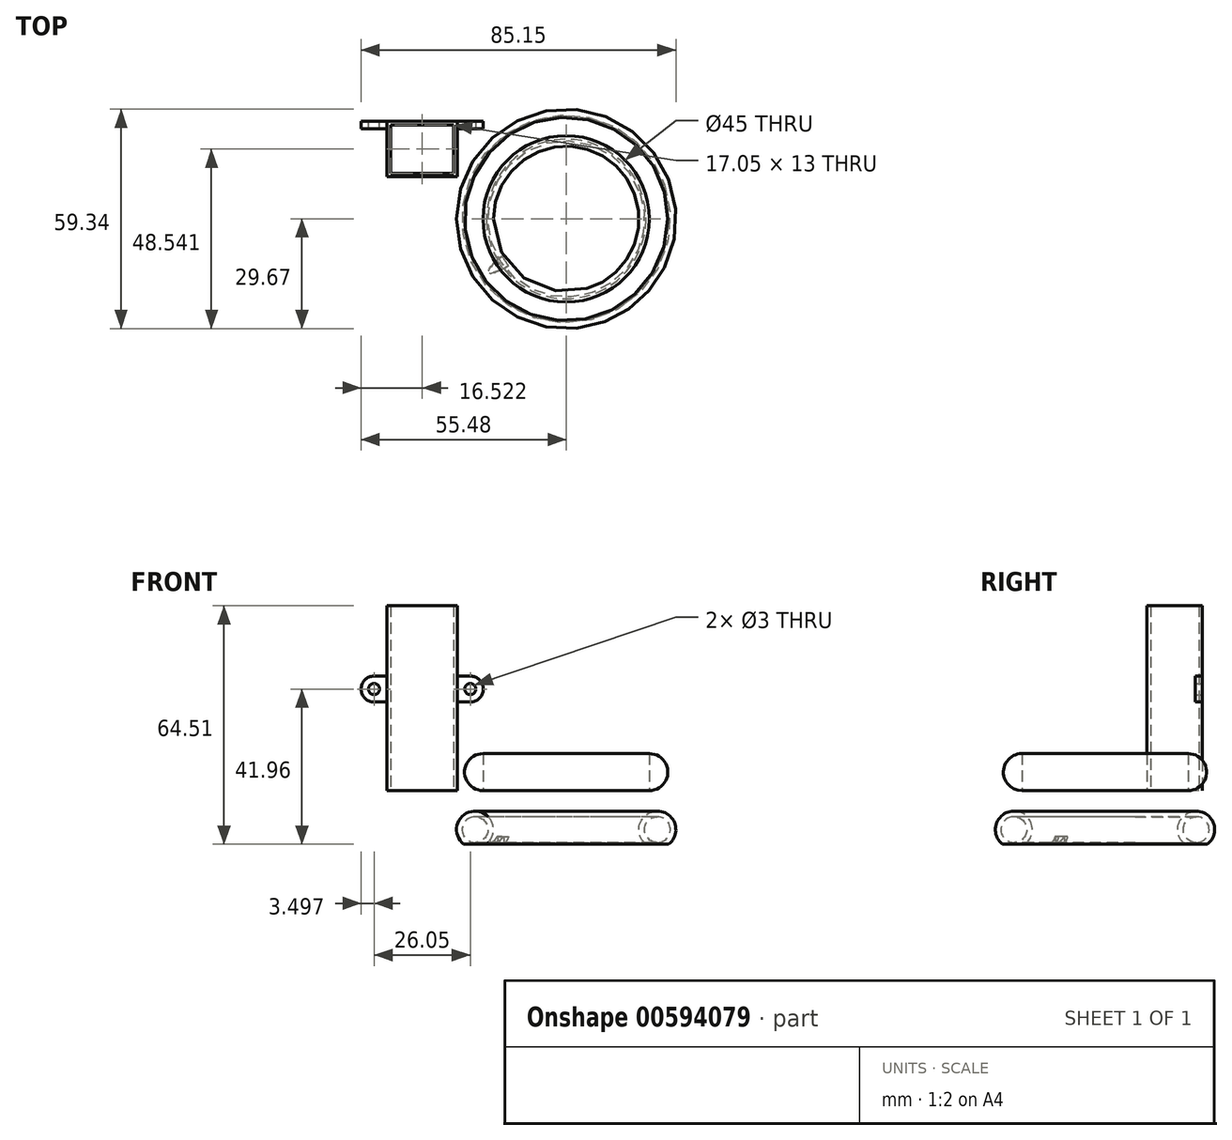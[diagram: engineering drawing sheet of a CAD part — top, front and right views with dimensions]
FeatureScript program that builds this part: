
annotation { "Feature Type Name" : "Feature", "Feature Type Description" : "" }
export const myFeature = defineFeature(function(context is Context, id is Id, definition is map)
    precondition{}
    {
        {
            var Q0;
            Q0=qCreatedBy(makeId("Top.planeOp"),FACE);
            var sketch = newSketch(context, id + "F0", { "sketchPlane" : qUnion([Q0])});
            skLineSegment(sketch, "E0.bottom", {"start": v(-48.48, 26.37) * mm, "end": v(-29.43, 26.37) * mm});
            skLineSegment(sketch, "E0.top", {"start": v(-48.48, 11.37) * mm, "end": v(-29.43, 11.37) * mm});
            skLineSegment(sketch, "E0.left", {"start": v(-48.48, 26.37) * mm, "end": v(-48.48, 11.37) * mm});
            skLineSegment(sketch, "E0.right", {"start": v(-29.43, 26.37) * mm, "end": v(-29.43, 11.37) * mm});
            skSolve(sketch);
        }
        {
            var Q0;
            Q0=makeQuery(id+"F0.imprint","IMPRINT",FACE,{"disambiguationData":[TD([[makeQuery(id+"F0.imprint","IMPRINT",EDGE,{"derivedFrom":sQuery(id+"F0.wireOp",EDGE,"E0.bottom")}),-1.0]])]});
            extrude(context, id + "F1", {"entities" : qUnion([Q0]), "depth" : 50 * mm, "offsetDistance" : 25 * mm});
        }
        {
            var Q0;
            Q0=makeQuery(id+"F1.opExtrude","CAP_FACE",FACE,{"disambiguationData":[OSD([sQuery(id+"F0.wireOp",EDGE,"E0.bottom"),sQuery(id+"F0.wireOp",EDGE,"E0.top"),sQuery(id+"F0.wireOp",EDGE,"E0.left"),sQuery(id+"F0.wireOp",EDGE,"E0.right")])],"isStart":false});
            var Q1;
            Q1=makeQuery(id+"F1.opExtrude","CAP_FACE",FACE,{"disambiguationData":[OSD([sQuery(id+"F0.wireOp",EDGE,"E0.bottom"),sQuery(id+"F0.wireOp",EDGE,"E0.top"),sQuery(id+"F0.wireOp",EDGE,"E0.left"),sQuery(id+"F0.wireOp",EDGE,"E0.right")])],"isStart":true});
            shell(context, id + "F2", {"entities" : qUnion([Q0, Q1]), "thickness" : 1 * mm});
        }
        {
            var Q0;
            Q0=makeQuery(id+"F1.opExtrude","SWEPT_FACE",FACE,{"disambiguationData":[OSD([sQuery(id+"F0.wireOp",EDGE,"E0.left")])]});
            var sketch = newSketch(context, id + "F3", { "sketchPlane" : qUnion([Q0])});
            skLineSegment(sketch, "E1", {"start": v(-26.37, 50) * mm, "end": v(-26.37, 30.95) * mm, "construction": true});
            skLineSegment(sketch, "E2", {"start": v(-26.37, 30.95) * mm, "end": v(-26.37, 23.95) * mm});
            skLineSegment(sketch, "E3", {"start": v(-26.37, 30.95) * mm, "end": v(-24.37, 30.95) * mm});
            skLineSegment(sketch, "E4", {"start": v(-24.37, 30.95) * mm, "end": v(-24.37, 23.95) * mm});
            skLineSegment(sketch, "E5", {"start": v(-24.37, 23.95) * mm, "end": v(-26.37, 23.95) * mm});
            skSolve(sketch);
        }
        {
            var Q0;
            Q0=makeQuery(id+"F3.imprint","IMPRINT",FACE,{"disambiguationData":[TD([[makeQuery(id+"F3.imprint","IMPRINT",EDGE,{"derivedFrom":sQuery(id+"F3.wireOp",EDGE,"E2")}),1.0]])]});
            extrude(context, id + "F4", {"entities" : qUnion([Q0]), "operationType" : NewBodyOperationType.ADD, "depth" : 7 * mm, "offsetDistance" : 25 * mm});
        }
        {
            var Q0;
            Q0=makeQuery(id+"F4.opExtrude","CAP_EDGE",EDGE,{"disambiguationData":[OSD([sQuery(id+"F3.wireOp",EDGE,"E3")])],"isStart":false});
            var Q1;
            Q1=makeQuery(id+"F4.opExtrude","CAP_EDGE",EDGE,{"disambiguationData":[OSD([sQuery(id+"F3.wireOp",EDGE,"E5")])],"isStart":false});
            fillet(context, id + "F5", {"entities" : qUnion([Q0, Q1]), "radius" : 3.5 * mm, "tangentPropagation" : true, "allowEdgeOverflow" : false});
        }
        {
            var Q0;
            Q0=makeQuery(id+"F1.opExtrude","SWEPT_FACE",FACE,{"disambiguationData":[OSD([sQuery(id+"F0.wireOp",EDGE,"E0.right")])]});
            var sketch = newSketch(context, id + "F6", { "sketchPlane" : qUnion([Q0])});
            skLineSegment(sketch, "E6", {"start": v(26.37, 50) * mm, "end": v(26.37, 30.95) * mm, "construction": true});
            skLineSegment(sketch, "E7", {"start": v(26.37, 30.95) * mm, "end": v(26.37, 23.95) * mm});
            skLineSegment(sketch, "E8", {"start": v(26.37, 23.95) * mm, "end": v(24.37, 23.95) * mm});
            skLineSegment(sketch, "E9", {"start": v(24.37, 23.95) * mm, "end": v(24.37, 30.95) * mm});
            skLineSegment(sketch, "E10", {"start": v(24.37, 30.95) * mm, "end": v(26.37, 30.95) * mm});
            skSolve(sketch);
        }
        {
            var Q0;
            Q0=makeQuery(id+"F6.imprint","IMPRINT",FACE,{"disambiguationData":[TD([[makeQuery(id+"F6.imprint","IMPRINT",EDGE,{"derivedFrom":sQuery(id+"F6.wireOp",EDGE,"E7")}),-1.0]])]});
            extrude(context, id + "F7", {"entities" : qUnion([Q0]), "operationType" : NewBodyOperationType.ADD, "depth" : 7 * mm, "offsetDistance" : 25 * mm});
        }
        {
            var Q0;
            Q0=makeQuery(id+"F7.opExtrude","CAP_EDGE",EDGE,{"disambiguationData":[OSD([sQuery(id+"F6.wireOp",EDGE,"E10")])],"isStart":false});
            var Q1;
            Q1=makeQuery(id+"F7.opExtrude","CAP_EDGE",EDGE,{"disambiguationData":[OSD([sQuery(id+"F6.wireOp",EDGE,"E8")])],"isStart":false});
            fillet(context, id + "F8", {"entities" : qUnion([Q0, Q1]), "radius" : 3.5 * mm, "tangentPropagation" : true, "allowEdgeOverflow" : false});
        }
        {
            var Q0;
            Q0=makeQuery(id+"F7.boolean.opBoolean","MERGE",FACE,{"derivedFrom":[makeQuery(id+"F4.boolean.opBoolean","MERGE",FACE,{"derivedFrom":[makeQuery(id+"F1.opExtrude","SWEPT_FACE",FACE,{"disambiguationData":[OSD([sQuery(id+"F0.wireOp",EDGE,"E0.bottom")])]}),makeQuery(id+"F4.opExtrude","SWEPT_FACE",FACE,{"disambiguationData":[OSD([sQuery(id+"F3.wireOp",EDGE,"E2")])]})]}),makeQuery(id+"F7.opExtrude","SWEPT_FACE",FACE,{"disambiguationData":[OSD([sQuery(id+"F6.wireOp",EDGE,"E7")])]})]});
            var sketch = newSketch(context, id + "F9", { "sketchPlane" : qUnion([Q0])});
            skCircle(sketch, "E11", {"center": v(25.93, 27.45) * mm, "radius": 1.5 * mm});
            skCircle(sketch, "E12", {"center": v(51.98, 27.45) * mm, "radius": 1.5 * mm});
            skSolve(sketch);
        }
        {
            var Q0;
            Q0=makeQuery(id+"F9.imprint","IMPRINT",FACE,{"disambiguationData":[TD([[makeQuery(id+"F9.imprint","IMPRINT",EDGE,{"derivedFrom":sQuery(id+"F9.wireOp",EDGE,"E11")}),1.0]])]});
            var Q1;
            Q1=makeQuery(id+"F9.imprint","IMPRINT",FACE,{"disambiguationData":[TD([[makeQuery(id+"F9.imprint","IMPRINT",EDGE,{"derivedFrom":sQuery(id+"F9.wireOp",EDGE,"E12")}),1.0]])]});
            extrude(context, id + "F10", {"entities" : qUnion([Q0, Q1]), "operationType" : NewBodyOperationType.REMOVE, "oppositeDirection" : true, "depth" : 25 * mm, "offsetDistance" : 25 * mm});
        }
        {
            var Q0;
            Q0=qCreatedBy(makeId("Top.planeOp"),FACE);
            var sketch = newSketch(context, id + "F11", { "sketchPlane" : qUnion([Q0])});
            skCircle(sketch, "E13", {"center": v(0, 0) * mm, "radius": 27.5 * mm});
            skCircle(sketch, "E14", {"center": v(0, 0) * mm, "radius": 22.5 * mm});
            skSolve(sketch);
        }
        {
            var Q0;
            Q0=makeQuery(id+"F11.imprint","IMPRINT",FACE,{"disambiguationData":[TD([[makeQuery(id+"F11.imprint","IMPRINT",EDGE,{"derivedFrom":sQuery(id+"F11.wireOp",EDGE,"E13")}),1.0]])]});
            extrude(context, id + "F12", {"entities" : qUnion([Q0]), "depth" : 10 * mm, "offsetDistance" : 25 * mm});
        }
        {
            var Q0;
            Q0=makeQuery(id+"F12.opExtrude","CAP_EDGE",EDGE,{"disambiguationData":[OSD([sQuery(id+"F11.wireOp",EDGE,"E13")])],"isStart":false});
            var Q1;
            Q1=makeQuery(id+"F12.opExtrude","CAP_EDGE",EDGE,{"disambiguationData":[OSD([sQuery(id+"F11.wireOp",EDGE,"E13")])],"isStart":true});
            fillet(context, id + "F13", {"entities" : qUnion([Q0, Q1]), "radius" : 5 * mm, "tangentPropagation" : true, "allowEdgeOverflow" : false});
        }
        {
            var Q0;
            Q0=qCreatedBy(makeId("Right.planeOp"),FACE);
            var sketch = newSketch(context, id + "F14", { "sketchPlane" : qUnion([Q0])});
            skLineSegment(sketch, "E15", {"start": v(-24.67, -5.57) * mm, "end": v(-24.67, -15.57) * mm, "construction": true});
            skArc(sketch, "E16", {"start": v(-24.67, -5.57) * mm, "mid": v(-29.67, -10.57) * mm, "end": v(-24.67, -15.57) * mm});
            skLineSegment(sketch, "E17", {"start": v(-24.67, -5.57) * mm, "end": v(-24.67, -7.07) * mm, "construction": true});
            skLineSegment(sketch, "E18", {"start": v(-24.67, -7.07) * mm, "end": v(-24.67, -14.07) * mm});
            skLineSegment(sketch, "E19", {"start": v(-24.67, -14.07) * mm, "end": v(-24.67, -15.57) * mm, "construction": true});
            skLineSegment(sketch, "E20", {"start": v(-29.67, -10.57) * mm, "end": v(-28.17, -10.57) * mm, "construction": true});
            skArc(sketch, "E21", {"start": v(-24.67, -7.07) * mm, "mid": v(-28.17, -10.57) * mm, "end": v(-24.67, -14.07) * mm});
            skLineSegment(sketch, "E22", {"start": v(-24.67, -14.07) * mm, "end": v(-24.67, -14.07) * mm});
            skLineSegment(sketch, "E23", {"start": v(-28.17, -10.57) * mm, "end": v(-24.67, -10.57) * mm, "construction": true});
            skLineSegment(sketch, "E24", {"start": v(-24.67, -15.57) * mm, "end": v(-24.67, -14.5) * mm});
            skLineSegment(sketch, "E25", {"start": v(-24.67, -14.5) * mm, "end": v(-27.75, -14.5) * mm});
            skLineSegment(sketch, "E26", {"start": v(-27.75, -14.5) * mm, "end": v(-27.75, -15.57) * mm});
            skLineSegment(sketch, "E27", {"start": v(-27.75, -15.57) * mm, "end": v(-24.67, -15.57) * mm});
            skLineSegment(sketch, "E28", {"start": v(-24.67, -10.57) * mm, "end": v(-21.17, -10.57) * mm});
            skLineSegment(sketch, "E29", {"start": v(-21.17, -10.57) * mm, "end": v(-19.67, -10.57) * mm, "construction": true});
            skArc(sketch, "E30", {"start": v(-24.67, -15.57) * mm, "mid": v(-19.67, -10.57) * mm, "end": v(-24.67, -5.57) * mm});
            skArc(sketch, "E31", {"start": v(-24.67, -14.07) * mm, "mid": v(-21.17, -10.57) * mm, "end": v(-24.67, -7.07) * mm});
            skLineSegment(sketch, "E32", {"start": v(-24.67, -14.5) * mm, "end": v(-21.59, -14.5) * mm});
            skLineSegment(sketch, "E33", {"start": v(-21.59, -14.5) * mm, "end": v(-21.59, -15.56) * mm});
            skLineSegment(sketch, "E34", {"start": v(-21.59, -15.56) * mm, "end": v(-24.67, -15.57) * mm});
            skSolve(sketch);
        }
        {
            var Q0;
            Q0=qCreatedBy(makeId("Top.planeOp"),FACE);
            var sketch = newSketch(context, id + "F15", { "sketchPlane" : qUnion([Q0])});
            skCircle(sketch, "E35", {"center": v(0, 0) * mm, "radius": 27.5 * mm});
            skPoint(sketch, "E35.first.point", {"position": v(27.5, 0) * mm});
            skPoint(sketch, "E35.second.point", {"position": v(23.42, 14.42) * mm});
            skPoint(sketch, "E35.third.point", {"position": v(25.68, 9.85) * mm});
            skSolve(sketch);
        }
        {
            var Q0;
            {var subQ5=sQuery(id+"F14.wireOp",EDGE,"E21");Q0=makeQuery(id+"F14.imprint","IMPRINT",FACE,{"disambiguationData":[TD([[makeQuery(id+"F14.imprint","IMPRINT",EDGE,{"derivedFrom":subQ5}),-1.0]])]});}
            var Q1;
            Q1=sQuery(id+"F15.wireOp",EDGE,"E35");
            revolve(context, id + "F16", {"entities" : qUnion([Q0]), "axis" : qUnion([Q1]), "revolveType" : RevolveType.FULL});
        }
        {
            var Q0;
            Q0=makeQuery(id+"F16.opRevolve","SWEPT_FACE",FACE,{"disambiguationData":[OSD([sQuery(id+"F14.wireOp",EDGE,"E25"),sQuery(id+"F14.wireOp",EDGE,"E32")])]});
            var sketch = newSketch(context, id + "F17", { "sketchPlane" : qUnion([Q0])});
            skFitSpline(sketch, "E36", {"points": [v(-18.57, 11) * mm, v(-21, 14.51) * mm, v(-16.86, 13.47) * mm], "startDerivative": vector(-9.95, 9.22) * mm, "endDerivative": vector(12.49, -5.5) * mm});
            skLineSegment(sketch, "E37", {"start": v(-16.86, 13.47) * mm, "end": v(-18.57, 11) * mm, "construction": true});
            skLineSegment(sketch, "E38", {"start": v(-17.72, 12.24) * mm, "end": v(-21, 14.51) * mm, "construction": true});
            skLineSegment(sketch, "E39", {"start": v(-16.86, 13.47) * mm, "end": v(-14.6, 11.91) * mm});
            skLineSegment(sketch, "E40", {"start": v(-14.6, 11.91) * mm, "end": v(-16.34, 9.4) * mm});
            skLineSegment(sketch, "E41", {"start": v(-16.34, 9.4) * mm, "end": v(-18.57, 11) * mm});
            skSolve(sketch);
        }
        {
            var Q0;
            {var subQ0=sQuery(id+"F17.wireOp",EDGE,"E36");Q0=makeQuery(id+"F17.imprint","IMPRINT",FACE,{"disambiguationData":[TD([[makeQuery(id+"F17.imprint","IMPRINT",EDGE,{"derivedFrom":subQ0}),-1.0]])]});}
            var Q1;
            {var subQ0=sQuery(id+"F17.wireOp",EDGE,"E39");Q1=makeQuery(id+"F17.imprint","IMPRINT",FACE,{"disambiguationData":[TD([[makeQuery(id+"F17.imprint","IMPRINT",EDGE,{"derivedFrom":subQ0}),-1.0]])]});}
            extrude(context, id + "F18", {"entities" : qUnion([Q0, Q1]), "operationType" : NewBodyOperationType.REMOVE, "oppositeDirection" : true, "depth" : 2 * mm, "offsetDistance" : 25 * mm});
        }
    });
